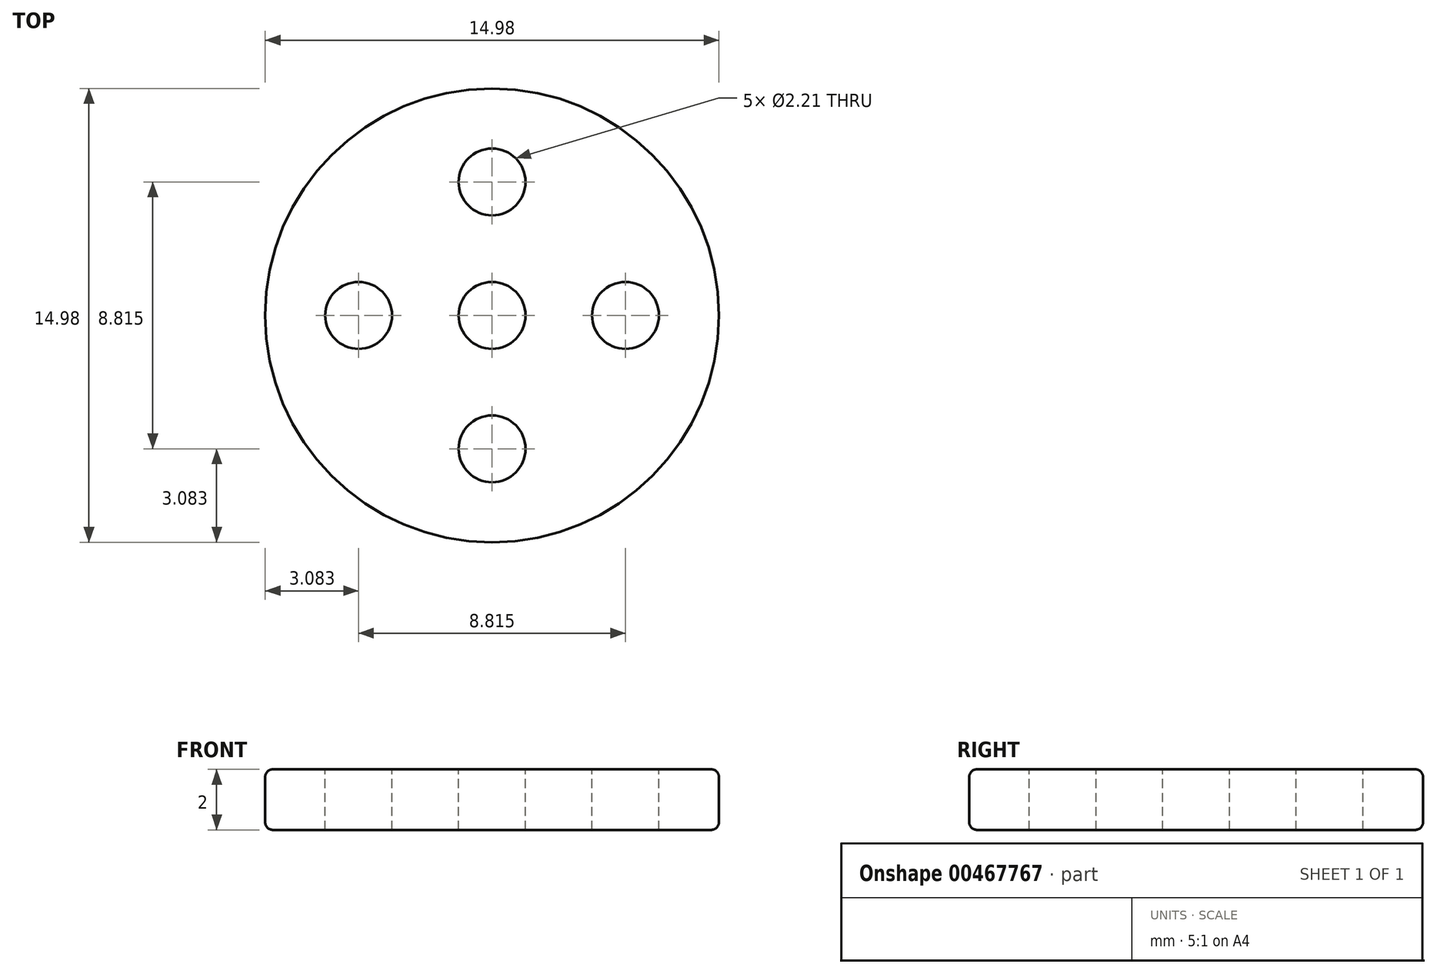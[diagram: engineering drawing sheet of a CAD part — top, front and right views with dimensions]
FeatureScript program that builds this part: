
annotation { "Feature Type Name" : "Feature", "Feature Type Description" : "" }
export const myFeature = defineFeature(function(context is Context, id is Id, definition is map)
    precondition{}
    {
        {
            var Q0;
            Q0=qCreatedBy(makeId("Top.planeOp"),FACE);
            var sketch = newSketch(context, id + "F0", { "sketchPlane" : qUnion([Q0])});
            skCircle(sketch, "E0", {"center": v(0, 0) * mm, "radius": 7.5 * mm});
            skSolve(sketch);
        }
        {
            var Q0;
            Q0 = qSketchRegion(id + "F0", true);
            extrude(context, id + "F1", {"entities" : qUnion([Q0]), "depth" : 2 * mm});
        }
        {
            var Q0;
            Q0=makeQuery(id+"F1.opExtrude","CAP_FACE",FACE,{"disambiguationData":[OSD([sQuery(id+"F0.wireOp",EDGE,"E0")])],"isStart":false});
            var sketch = newSketch(context, id + "F2", { "sketchPlane" : qUnion([Q0])});
            skCircle(sketch, "E1", {"center": v(-4.4, 0) * mm, "radius": 1.1 * mm});
            skCircle(sketch, "E2", {"center": v(0, 0) * mm, "radius": 1.1 * mm});
            skCircle(sketch, "E3", {"center": v(0, 4.4) * mm, "radius": 1.1 * mm});
            skCircle(sketch, "E4", {"center": v(4.4, 0) * mm, "radius": 1.1 * mm});
            skCircle(sketch, "E5", {"center": v(0, -4.4) * mm, "radius": 1.1 * mm});
            skSolve(sketch);
        }
        {
            var Q0;
            Q0 = qSketchRegion(id + "F2", true);
            extrude(context, id + "F3", {"entities" : qUnion([Q0]), "operationType" : NewBodyOperationType.REMOVE, "oppositeDirection" : true, "depth" : 25.4 * mm});
        }
        {
            var Q0;
            Q0=makeQuery(id+"F1.opExtrude","CAP_EDGE",EDGE,{"disambiguationData":[OSD([sQuery(id+"F0.wireOp",EDGE,"E0")])],"isStart":false});
            var Q1;
            Q1=makeQuery(id+"F1.opExtrude","CAP_EDGE",EDGE,{"disambiguationData":[OSD([sQuery(id+"F0.wireOp",EDGE,"E0")])],"isStart":true});
            fillet(context, id + "F4", {"entities" : qUnion([Q0, Q1]), "radius" : 0.25 * mm, "tangentPropagation" : true, "allowEdgeOverflow" : false});
        }
    });
